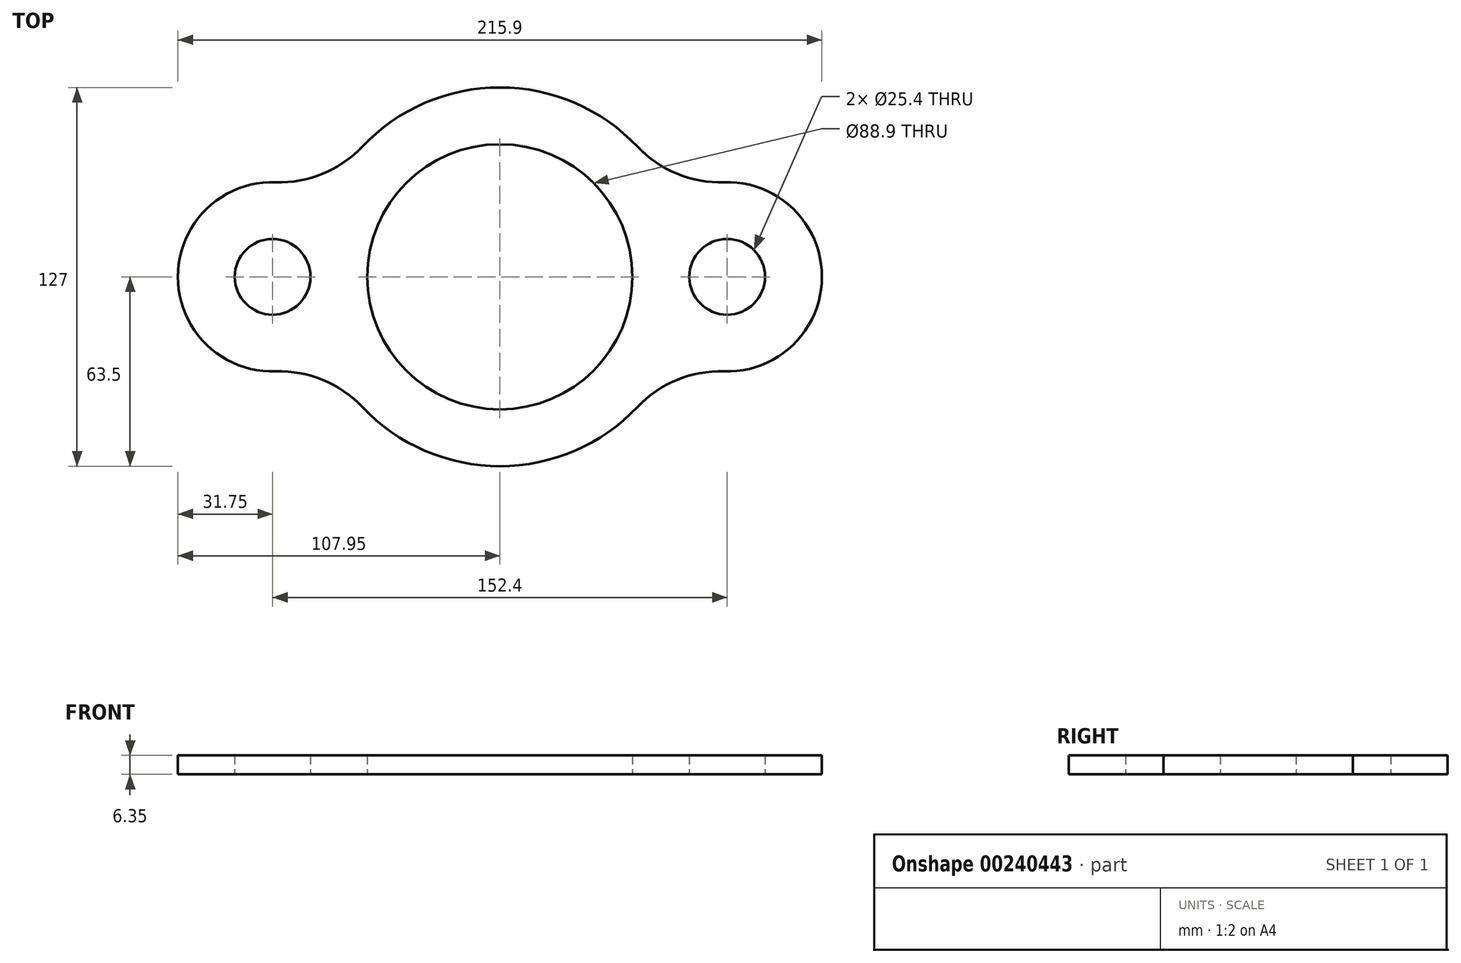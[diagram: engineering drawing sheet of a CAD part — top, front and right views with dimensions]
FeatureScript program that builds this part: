
annotation { "Feature Type Name" : "Feature", "Feature Type Description" : "" }
export const myFeature = defineFeature(function(context is Context, id is Id, definition is map)
    precondition{}
    {
        {
            var Q0;
            Q0=qCreatedBy(makeId("Top.planeOp"),FACE);
            var sketch = newSketch(context, id + "F0", { "sketchPlane" : qUnion([Q0])});
            skCircle(sketch, "E0", {"center": v(0, 0) * mm, "radius": 44.45 * mm});
            skCircle(sketch, "E1", {"center": v(-76.2, 0) * mm, "radius": 12.7 * mm});
            skCircle(sketch, "E2", {"center": v(76.2, 0) * mm, "radius": 12.7 * mm});
            skArc(sketch, "E3", {"start": v(46.14, 43.63) * mm, "mid": v(0, 63.5) * mm, "end": v(-46.14, 43.63) * mm});
            skArc(sketch, "E4", {"start": v(75.12, -31.73) * mm, "mid": v(107.95, 0) * mm, "end": v(75.12, 31.73) * mm});
            skArc(sketch, "E5", {"start": v(-75.12, 31.73) * mm, "mid": v(-107.95, 0) * mm, "end": v(-75.12, -31.73) * mm});
            skArc(sketch, "E6.trimOffspring", {"start": v(-46.14, -43.63) * mm, "mid": v(0, -63.5) * mm, "end": v(46.14, -43.63) * mm});
            skArc(sketch, "E7.filletArc", {"start": v(-75.12, 31.73) * mm, "mid": v(-59.35, 34.56) * mm, "end": v(-46.14, 43.63) * mm});
            skArc(sketch, "E8.filletArc", {"start": v(46.14, 43.63) * mm, "mid": v(59.35, 34.56) * mm, "end": v(75.12, 31.73) * mm});
            skArc(sketch, "E9.filletArc", {"start": v(-46.14, -43.63) * mm, "mid": v(-59.35, -34.56) * mm, "end": v(-75.12, -31.73) * mm});
            skArc(sketch, "E10.filletArc", {"start": v(75.12, -31.73) * mm, "mid": v(59.35, -34.56) * mm, "end": v(46.14, -43.63) * mm});
            skSolve(sketch);
        }
        {
            var Q0;
            Q0=makeQuery(id+"F0.imprint","IMPRINT",FACE,{"disambiguationData":[TD([[makeQuery(id+"F0.imprint","IMPRINT",EDGE,{"derivedFrom":sQuery(id+"F0.wireOp",EDGE,"E0")}),-1.0]])]});
            extrude(context, id + "F1", {"entities" : qUnion([Q0]), "depth" : 6.35 * mm});
        }
        {
            var Q0;
            Q0=makeQuery(id+"F0.imprint","IMPRINT",FACE,{"disambiguationData":[TD([[makeQuery(id+"F0.imprint","IMPRINT",EDGE,{"derivedFrom":sQuery(id+"F0.wireOp",EDGE,"E0")}),1.0]])]});
            extrude(context, id + "F2", {"entities" : qUnion([Q0]), "operationType" : NewBodyOperationType.REMOVE, "endBound" : BoundingType.THROUGH_ALL, "oppositeDirection" : true, "depth" : 25.4 * mm});
        }
    });
